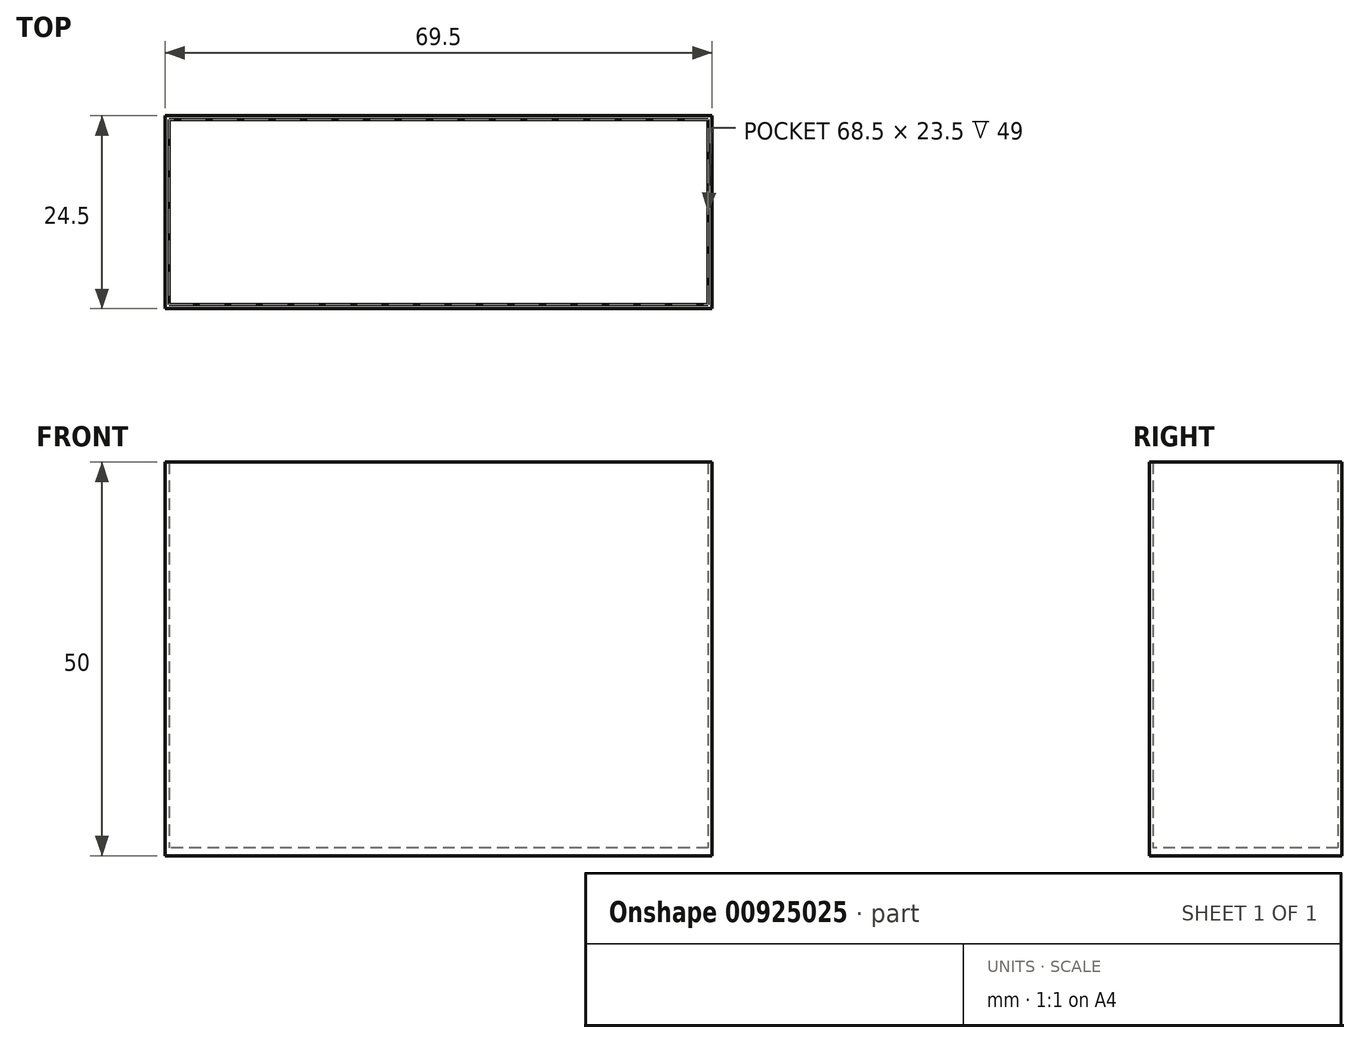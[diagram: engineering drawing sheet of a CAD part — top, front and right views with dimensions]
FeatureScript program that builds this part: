
annotation { "Feature Type Name" : "Feature", "Feature Type Description" : "" }
export const myFeature = defineFeature(function(context is Context, id is Id, definition is map)
    precondition{}
    {
        {
            var Q0;
            Q0=qCreatedBy(makeId("Top.planeOp"),FACE);
            var sketch = newSketch(context, id + "F0", { "sketchPlane" : qUnion([Q0])});
            skLineSegment(sketch, "E0.bottom", {"start": v(34.25, 11.75) * mm, "end": v(-34.25, 11.75) * mm});
            skLineSegment(sketch, "E0.top", {"start": v(34.25, -11.75) * mm, "end": v(-34.25, -11.75) * mm});
            skLineSegment(sketch, "E0.left", {"start": v(34.25, 11.75) * mm, "end": v(34.25, -11.75) * mm});
            skLineSegment(sketch, "E0.right", {"start": v(-34.25, 11.75) * mm, "end": v(-34.25, -11.75) * mm});
            skPoint(sketch, "E0.middle", {"position": v(0, 0) * mm});
            skLineSegment(sketch, "E1.bottom", {"start": v(-34.75, 12.25) * mm, "end": v(34.75, 12.25) * mm});
            skLineSegment(sketch, "E1.top", {"start": v(-34.75, -12.25) * mm, "end": v(34.75, -12.25) * mm});
            skLineSegment(sketch, "E1.left", {"start": v(-34.75, 12.25) * mm, "end": v(-34.75, -12.25) * mm});
            skLineSegment(sketch, "E1.right", {"start": v(34.75, 12.25) * mm, "end": v(34.75, -12.25) * mm});
            skSolve(sketch);
        }
        {
            var Q0;
            Q0=makeQuery(id+"F0.imprint","IMPRINT",FACE,{"disambiguationData":[TD([[makeQuery(id+"F0.imprint","IMPRINT",EDGE,{"derivedFrom":sQuery(id+"F0.wireOp",EDGE,"E0.bottom")}),1.0]])]});
            extrude(context, id + "F1", {"entities" : qUnion([Q0]), "depth" : 1 * mm, "offsetDistance" : 25 * mm});
        }
        {
            var Q0;
            Q0=qCreatedBy(makeId("Top.planeOp"),FACE);
            var sketch = newSketch(context, id + "F2", { "sketchPlane" : qUnion([Q0])});
            skLineSegment(sketch, "E2.bottom", {"start": v(-34.25, 11.75) * mm, "end": v(34.25, 11.75) * mm});
            skLineSegment(sketch, "E2.top", {"start": v(-34.25, -11.75) * mm, "end": v(34.25, -11.75) * mm});
            skLineSegment(sketch, "E2.left", {"start": v(-34.25, 11.75) * mm, "end": v(-34.25, -11.75) * mm});
            skLineSegment(sketch, "E2.right", {"start": v(34.25, 11.75) * mm, "end": v(34.25, -11.75) * mm});
            skPoint(sketch, "E2.middle", {"position": v(0, 0) * mm});
            skLineSegment(sketch, "E3.bottom", {"start": v(-34.75, 12.25) * mm, "end": v(34.75, 12.25) * mm});
            skLineSegment(sketch, "E3.top", {"start": v(-34.75, -12.25) * mm, "end": v(34.75, -12.25) * mm});
            skLineSegment(sketch, "E3.left", {"start": v(-34.75, 12.25) * mm, "end": v(-34.75, -12.25) * mm});
            skLineSegment(sketch, "E3.right", {"start": v(34.75, 12.25) * mm, "end": v(34.75, -12.25) * mm});
            skSolve(sketch);
        }
        {
            var Q0;
            Q0 = qSketchRegion(id + "F2", true);
            extrude(context, id + "F3", {"entities" : qUnion([Q0]), "operationType" : NewBodyOperationType.ADD, "depth" : 50 * mm, "offsetDistance" : 25 * mm});
        }
    });
